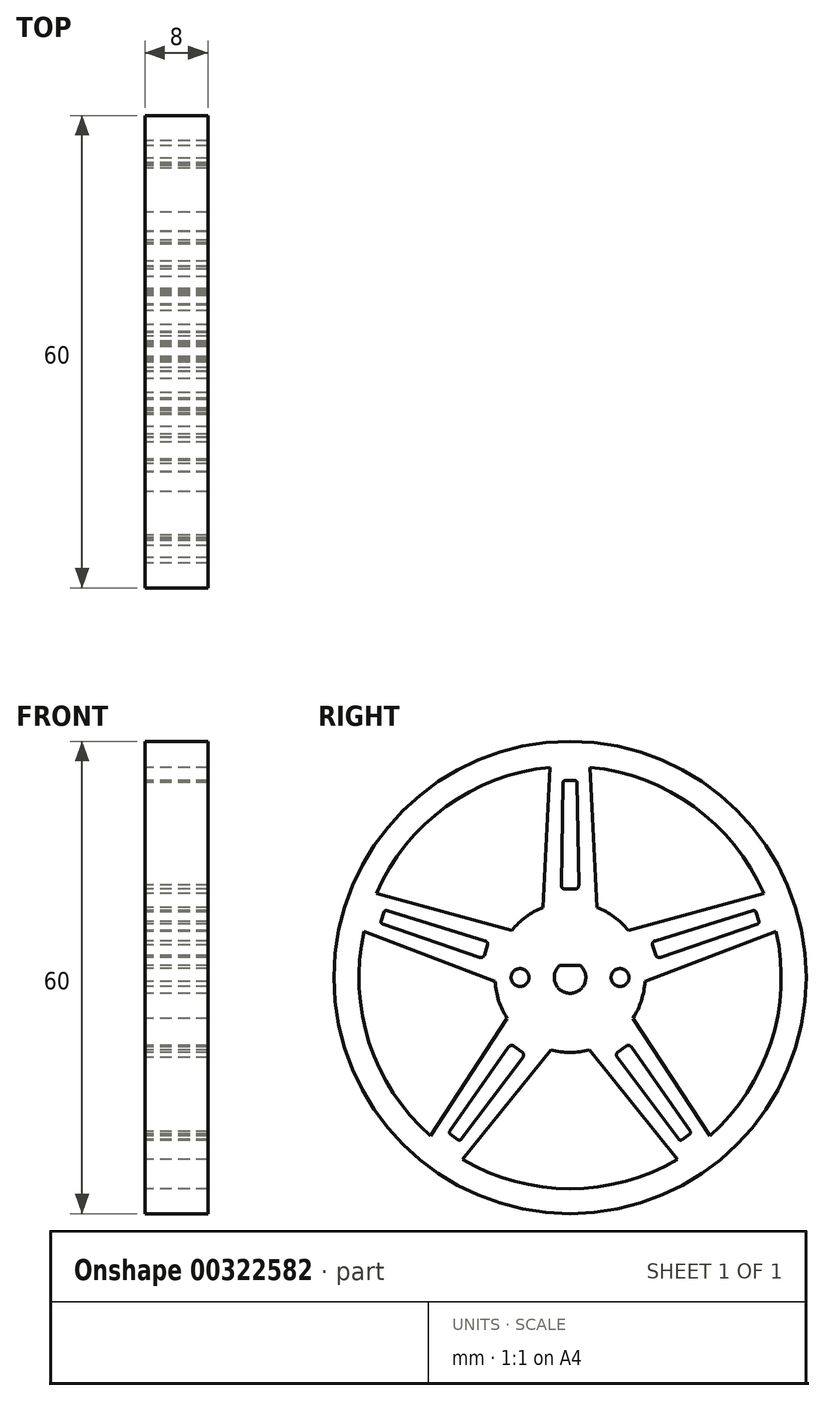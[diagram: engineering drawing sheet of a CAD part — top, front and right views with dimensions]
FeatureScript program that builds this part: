
annotation { "Feature Type Name" : "Feature", "Feature Type Description" : "" }
export const myFeature = defineFeature(function(context is Context, id is Id, definition is map)
    precondition{}
    {
        {
            var Q0;
            Q0=qCreatedBy(makeId("Right.planeOp"),FACE);
            var sketch = newSketch(context, id + "F0", { "sketchPlane" : qUnion([Q0])});
            skCircle(sketch, "E0", {"center": v(0, 0) * mm, "radius": 30 * mm});
            skArc(sketch, "E1", {"start": v(-2.54, 26.7) * mm, "mid": v(-15.77, 21.7) * mm, "end": v(-24.61, 10.67) * mm});
            skArc(sketch, "E2", {"start": v(-3.43, 8.89) * mm, "mid": v(-5.6, 7.7) * mm, "end": v(-7.4, 6) * mm});
            skCircle(sketch, "E3", {"center": v(-6.35, 0) * mm, "radius": 1.13 * mm});
            skCircle(sketch, "E4.MirrorC", {"center": v(6.35, 0) * mm, "radius": 1.13 * mm});
            skLineSegment(sketch, "E5", {"start": v(0, 0) * mm, "end": v(0, 30) * mm, "construction": true});
            skLineSegment(sketch, "E6.1.0", {"start": v(0, 0) * mm, "end": v(-28.53, 9.27) * mm, "construction": true});
            skLineSegment(sketch, "E6.2.0", {"start": v(0, 0) * mm, "end": v(-17.63, -24.27) * mm, "construction": true});
            skLineSegment(sketch, "E6.3.0", {"start": v(0, 0) * mm, "end": v(17.63, -24.27) * mm, "construction": true});
            skLineSegment(sketch, "E6.4.0", {"start": v(0, 0) * mm, "end": v(28.53, 9.27) * mm, "construction": true});
            skLineSegment(sketch, "E7", {"start": v(-0.85, 26.8) * mm, "end": v(0.85, 26.8) * mm, "construction": true});
            skLineSegment(sketch, "E8", {"start": v(-1.14, 9.46) * mm, "end": v(1.14, 9.46) * mm, "construction": true});
            skLineSegment(sketch, "E9", {"start": v(-1.14, 9.46) * mm, "end": v(-1.11, 11.23) * mm, "construction": true});
            skLineSegment(sketch, "E10", {"start": v(0.85, 26.8) * mm, "end": v(0.88, 25.03) * mm, "construction": true});
            skLineSegment(sketch, "E11", {"start": v(-3.43, 8.89) * mm, "end": v(3.43, 8.89) * mm, "construction": true});
            skLineSegment(sketch, "E12", {"start": v(-2.54, 26.7) * mm, "end": v(2.54, 26.7) * mm, "construction": true});
            skLineSegment(sketch, "E13", {"start": v(-3.43, 8.89) * mm, "end": v(-2.54, 26.7) * mm});
            skLineSegment(sketch, "E14", {"start": v(2.54, 26.7) * mm, "end": v(3.43, 8.89) * mm});
            skLineSegment(sketch, "E15", {"start": v(-0.68, 11.23) * mm, "end": v(0.68, 11.23) * mm});
            skLineSegment(sketch, "E16", {"start": v(1.1, 11.69) * mm, "end": v(0.89, 24.78) * mm});
            skLineSegment(sketch, "E17", {"start": v(0.63, 25.03) * mm, "end": v(-0.63, 25.03) * mm});
            skLineSegment(sketch, "E18", {"start": v(-0.89, 24.78) * mm, "end": v(-1.1, 11.69) * mm});
            skArc(sketch, "E19", {"start": v(-0.63, 25.03) * mm, "mid": v(-0.8, 24.95) * mm, "end": v(-0.89, 24.78) * mm});
            skArc(sketch, "E20.MirrorCS", {"start": v(0.63, 25.03) * mm, "mid": v(0.8, 24.95) * mm, "end": v(0.89, 24.78) * mm});
            skArc(sketch, "E21", {"start": v(-1.1, 11.74) * mm, "mid": v(-1, 11.4) * mm, "end": v(-0.68, 11.23) * mm});
            skArc(sketch, "E22.MirrorCS", {"start": v(1.1, 11.74) * mm, "mid": v(1, 11.4) * mm, "end": v(0.68, 11.23) * mm});
            skLineSegment(sketch, "E23.trimOffspring", {"start": v(-1.1, 11.69) * mm, "end": v(-0.89, 24.78) * mm, "construction": true});
            skLineSegment(sketch, "E24.trimOffspring", {"start": v(1.11, 11.23) * mm, "end": v(1.14, 9.46) * mm, "construction": true});
            skLineSegment(sketch, "E25.trimOffspring", {"start": v(-0.88, 25.03) * mm, "end": v(-0.85, 26.8) * mm, "construction": true});
            skLineSegment(sketch, "E26.trimOffspring", {"start": v(0.89, 24.78) * mm, "end": v(1.1, 11.69) * mm, "construction": true});
            skArc(sketch, "E27.trimOffspring", {"start": v(0.85, 26.8) * mm, "mid": v(0, 26.82) * mm, "end": v(-0.85, 26.8) * mm, "construction": true});
            skLineSegment(sketch, "E28.1.0", {"start": v(-9.51, -0.52) * mm, "end": v(-26.18, 5.84) * mm});
            skLineSegment(sketch, "E28.1.1", {"start": v(-11.45, 2.56) * mm, "end": v(-23.84, 6.82) * mm});
            skLineSegment(sketch, "E28.1.2", {"start": v(-23.3, 8.5) * mm, "end": v(-10.77, 4.66) * mm});
            skLineSegment(sketch, "E28.1.3", {"start": v(-24.61, 10.67) * mm, "end": v(-7.4, 6) * mm});
            skLineSegment(sketch, "E28.1.4", {"start": v(-23.61, 8.33) * mm, "end": v(-24, 7.14) * mm});
            skArc(sketch, "E28.1.5", {"start": v(-23.61, 8.33) * mm, "mid": v(-23.48, 8.48) * mm, "end": v(-23.3, 8.5) * mm});
            skArc(sketch, "E28.1.6", {"start": v(-24, 7.14) * mm, "mid": v(-23.98, 6.95) * mm, "end": v(-23.84, 6.82) * mm});
            skArc(sketch, "E28.1.7", {"start": v(-10.82, 4.68) * mm, "mid": v(-10.53, 4.47) * mm, "end": v(-10.47, 4.12) * mm});
            skLineSegment(sketch, "E28.1.8", {"start": v(-10.9, 2.82) * mm, "end": v(-10.47, 4.12) * mm});
            skArc(sketch, "E28.1.9", {"start": v(-11.5, 2.58) * mm, "mid": v(-11.15, 2.58) * mm, "end": v(-10.9, 2.82) * mm});
            skLineSegment(sketch, "E28.2.0", {"start": v(-2.45, -9.2) * mm, "end": v(-13.64, -23.1) * mm});
            skLineSegment(sketch, "E28.2.1", {"start": v(-5.97, -10.1) * mm, "end": v(-13.85, -20.57) * mm});
            skLineSegment(sketch, "E28.2.2", {"start": v(-15.28, -19.53) * mm, "end": v(-7.76, -8.8) * mm});
            skLineSegment(sketch, "E28.2.3", {"start": v(-17.75, -20.1) * mm, "end": v(-8, -5.17) * mm});
            skLineSegment(sketch, "E28.2.4", {"start": v(-15.22, -19.88) * mm, "end": v(-14.2, -20.62) * mm});
            skArc(sketch, "E28.2.5", {"start": v(-15.22, -19.88) * mm, "mid": v(-15.32, -19.72) * mm, "end": v(-15.28, -19.53) * mm});
            skArc(sketch, "E28.2.6", {"start": v(-14.2, -20.62) * mm, "mid": v(-14.02, -20.66) * mm, "end": v(-13.85, -20.57) * mm});
            skArc(sketch, "E28.2.7", {"start": v(-7.8, -8.85) * mm, "mid": v(-7.5, -8.64) * mm, "end": v(-7.15, -8.69) * mm});
            skLineSegment(sketch, "E28.2.8", {"start": v(-6.05, -9.49) * mm, "end": v(-7.15, -8.69) * mm});
            skArc(sketch, "E28.2.9", {"start": v(-6, -10.14) * mm, "mid": v(-5.9, -9.8) * mm, "end": v(-6.05, -9.49) * mm});
            skLineSegment(sketch, "E29.1.3.0", {"start": v(8, -5.17) * mm, "end": v(17.75, -20.1) * mm});
            skLineSegment(sketch, "E29.3.3.0", {"start": v(7.76, -8.8) * mm, "end": v(15.28, -19.53) * mm});
            skLineSegment(sketch, "E29.6.3.0", {"start": v(13.85, -20.57) * mm, "end": v(5.97, -10.1) * mm});
            skLineSegment(sketch, "E29.9.3.0", {"start": v(13.64, -23.1) * mm, "end": v(2.45, -9.2) * mm});
            skLineSegment(sketch, "E29.12.3.0", {"start": v(14.2, -20.62) * mm, "end": v(15.22, -19.88) * mm});
            skArc(sketch, "E29.15.3.0", {"start": v(14.2, -20.62) * mm, "mid": v(14.02, -20.66) * mm, "end": v(13.85, -20.57) * mm});
            skArc(sketch, "E29.19.3.0", {"start": v(15.22, -19.88) * mm, "mid": v(15.32, -19.72) * mm, "end": v(15.28, -19.53) * mm});
            skArc(sketch, "E29.23.3.0", {"start": v(6, -10.14) * mm, "mid": v(5.9, -9.8) * mm, "end": v(6.05, -9.49) * mm});
            skLineSegment(sketch, "E29.27.3.0", {"start": v(7.15, -8.69) * mm, "end": v(6.05, -9.49) * mm});
            skArc(sketch, "E29.30.3.0", {"start": v(7.8, -8.85) * mm, "mid": v(7.5, -8.64) * mm, "end": v(7.15, -8.69) * mm});
            skLineSegment(sketch, "E29.1.4.0", {"start": v(7.4, 6) * mm, "end": v(24.61, 10.67) * mm});
            skLineSegment(sketch, "E29.3.4.0", {"start": v(10.77, 4.66) * mm, "end": v(23.3, 8.5) * mm});
            skLineSegment(sketch, "E29.6.4.0", {"start": v(23.84, 6.82) * mm, "end": v(11.45, 2.56) * mm});
            skLineSegment(sketch, "E29.9.4.0", {"start": v(26.18, 5.84) * mm, "end": v(9.51, -0.52) * mm});
            skLineSegment(sketch, "E29.12.4.0", {"start": v(24, 7.14) * mm, "end": v(23.61, 8.33) * mm});
            skArc(sketch, "E29.15.4.0", {"start": v(24, 7.14) * mm, "mid": v(23.98, 6.95) * mm, "end": v(23.84, 6.82) * mm});
            skArc(sketch, "E29.19.4.0", {"start": v(23.61, 8.33) * mm, "mid": v(23.48, 8.48) * mm, "end": v(23.3, 8.5) * mm});
            skArc(sketch, "E29.23.4.0", {"start": v(11.5, 2.58) * mm, "mid": v(11.15, 2.58) * mm, "end": v(10.9, 2.82) * mm});
            skLineSegment(sketch, "E29.27.4.0", {"start": v(10.47, 4.12) * mm, "end": v(10.9, 2.82) * mm});
            skArc(sketch, "E29.30.4.0", {"start": v(10.82, 4.68) * mm, "mid": v(10.53, 4.47) * mm, "end": v(10.47, 4.12) * mm});
            skArc(sketch, "E30.trimOffspring", {"start": v(-26.18, 5.84) * mm, "mid": v(-25.5, -8.29) * mm, "end": v(-17.75, -20.1) * mm});
            skArc(sketch, "E31.trimOffspring", {"start": v(24.61, 10.67) * mm, "mid": v(15.77, 21.7) * mm, "end": v(2.54, 26.7) * mm});
            skArc(sketch, "E32.trimOffspring", {"start": v(7.4, 6) * mm, "mid": v(5.6, 7.7) * mm, "end": v(3.43, 8.89) * mm});
            skArc(sketch, "E33.trimOffspring", {"start": v(-9.51, -0.52) * mm, "mid": v(-9.06, -2.94) * mm, "end": v(-8, -5.17) * mm});
            skArc(sketch, "E34.trimOffspring", {"start": v(-2.45, -9.2) * mm, "mid": v(0, -9.53) * mm, "end": v(2.45, -9.2) * mm});
            skArc(sketch, "E35.trimOffspring", {"start": v(8, -5.17) * mm, "mid": v(9.06, -2.94) * mm, "end": v(9.51, -0.52) * mm});
            skArc(sketch, "E36.trimOffspring", {"start": v(-13.64, -23.1) * mm, "mid": v(0, -26.82) * mm, "end": v(13.64, -23.1) * mm});
            skArc(sketch, "E37.trimOffspring", {"start": v(17.75, -20.1) * mm, "mid": v(25.5, -8.29) * mm, "end": v(26.18, 5.84) * mm});
            skCircle(sketch, "E38", {"center": v(0, 0) * mm, "radius": 9.52 * mm, "construction": true});
            skArc(sketch, "E39", {"start": v(-1.32, 1.5) * mm, "mid": v(0, -2) * mm, "end": v(1.32, 1.5) * mm});
            skLineSegment(sketch, "E40", {"start": v(1.32, 1.5) * mm, "end": v(-1.32, 1.5) * mm});
            skSolve(sketch);
        }
        {
            var Q0;
            Q0 = qSketchRegion(id + "F0", true);
            extrude(context, id + "F1", {"entities" : qUnion([Q0]), "depth" : 8 * mm, "offsetDistance" : 25.4 * mm});
        }
    });
